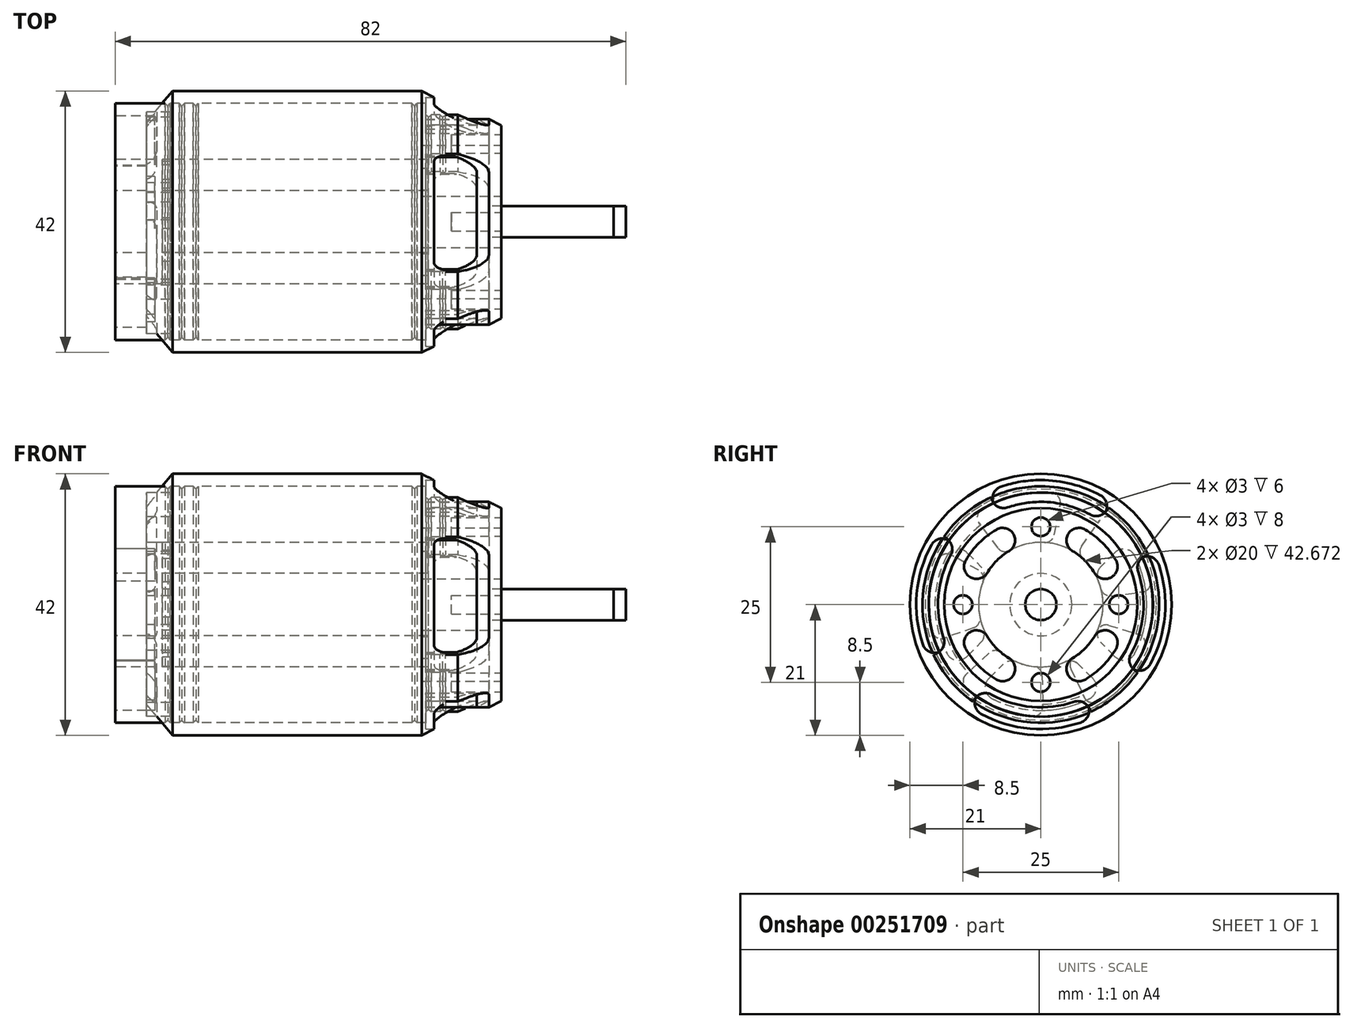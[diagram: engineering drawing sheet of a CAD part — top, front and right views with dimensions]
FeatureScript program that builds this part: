
annotation { "Feature Type Name" : "Feature", "Feature Type Description" : "" }
export const myFeature = defineFeature(function(context is Context, id is Id, definition is map)
    precondition{}
    {
        {
            var Q0;
            Q0=qCreatedBy(makeId("Top.planeOp"),FACE);
            var sketch = newSketch(context, id + "F0", { "sketchPlane" : qUnion([Q0])});
            skLineSegment(sketch, "E0", {"start": v(0, 0) * mm, "end": v(82, 0) * mm});
            skLineSegment(sketch, "E1", {"start": v(82, 0) * mm, "end": v(82, 2.5) * mm});
            skLineSegment(sketch, "E2", {"start": v(82, 2.5) * mm, "end": v(62, 2.5) * mm});
            skLineSegment(sketch, "E3", {"start": v(62, 2.5) * mm, "end": v(62, 15.5) * mm});
            skLineSegment(sketch, "E4", {"start": v(62, 15.5) * mm, "end": v(55, 19) * mm});
            skLineSegment(sketch, "E5", {"start": v(55, 19) * mm, "end": v(0, 19) * mm});
            skLineSegment(sketch, "E6", {"start": v(0, 19) * mm, "end": v(0, 0) * mm});
            skLineSegment(sketch, "E7", {"start": v(53, 19) * mm, "end": v(52.58, 18.58) * mm});
            skLineSegment(sketch, "E8", {"start": v(52.58, 18.58) * mm, "end": v(52.15, 19) * mm});
            skLineSegment(sketch, "E9.1.0.0", {"start": v(50.74, 19) * mm, "end": v(50.32, 18.58) * mm});
            skLineSegment(sketch, "E9.1.0.1", {"start": v(50.32, 18.58) * mm, "end": v(49.9, 19) * mm});
            skLineSegment(sketch, "E9.2.0.0", {"start": v(48.48, 19) * mm, "end": v(48.05, 18.58) * mm});
            skLineSegment(sketch, "E9.2.0.1", {"start": v(48.05, 18.58) * mm, "end": v(47.63, 19) * mm});
            skLineSegment(sketch, "E9.direction1", {"start": v(52.58, 18.58) * mm, "end": v(50.32, 18.58) * mm, "construction": true});
            skLineSegment(sketch, "E10", {"start": v(6, 19) * mm, "end": v(6, 0) * mm, "construction": true});
            skLineSegment(sketch, "E11", {"start": v(30.5, 19) * mm, "end": v(30.5, 0) * mm, "construction": true});
            skLineSegment(sketch, "E12.MirrorCS", {"start": v(8, 19) * mm, "end": v(8.42, 18.58) * mm});
            skLineSegment(sketch, "E13.MirrorCS", {"start": v(8.42, 18.58) * mm, "end": v(8.85, 19) * mm});
            skLineSegment(sketch, "E14.MirrorCS", {"start": v(10.26, 19) * mm, "end": v(10.68, 18.58) * mm});
            skLineSegment(sketch, "E15.MirrorCS", {"start": v(10.68, 18.58) * mm, "end": v(11.1, 19) * mm});
            skLineSegment(sketch, "E16.MirrorCS", {"start": v(12.52, 19) * mm, "end": v(12.95, 18.58) * mm});
            skLineSegment(sketch, "E17.MirrorCS", {"start": v(12.95, 18.58) * mm, "end": v(13.37, 19) * mm});
            skSolve(sketch);
        }
        {
            var Q0;
            Q0=makeQuery(id+"F0.imprint","IMPRINT",FACE,{"disambiguationData":[TD([[makeQuery(id+"F0.imprint","IMPRINT",EDGE,{"derivedFrom":sQuery(id+"F0.wireOp",EDGE,"E0")}),1.0]])]});
            var Q1;
            Q1=sQuery(id+"F0.wireOp",EDGE,"E0");
            revolve(context, id + "F1", {"entities" : qUnion([Q0]), "axis" : qUnion([Q1]), "revolveType" : RevolveType.FULL});
        }
        {
            var Q0;
            Q0=makeQuery(id+"F1.opRevolve","SWEPT_FACE",FACE,{"disambiguationData":[OSD([sQuery(id+"F0.wireOp",EDGE,"E3")])]});
            var sketch = newSketch(context, id + "F2", { "sketchPlane" : qUnion([Q0])});
            skCircle(sketch, "E18", {"center": v(0, 0) * mm, "radius": 12.5 * mm, "construction": true});
            skCircle(sketch, "E19", {"center": v(0, 12.5) * mm, "radius": 1.5 * mm});
            skCircle(sketch, "E20.1.0", {"center": v(-12.5, 0) * mm, "radius": 1.5 * mm});
            skCircle(sketch, "E20.2.0", {"center": v(0, -12.5) * mm, "radius": 1.5 * mm});
            skCircle(sketch, "E20.3.0", {"center": v(12.5, 0) * mm, "radius": 1.5 * mm});
            skCircle(sketch, "E21", {"center": v(0, 0) * mm, "radius": 14 * mm});
            skCircle(sketch, "E22", {"center": v(0, 0) * mm, "radius": 10 * mm});
            skLineSegment(sketch, "E23", {"start": v(-9.33, 3.6) * mm, "end": v(-13.06, 5.04) * mm});
            skLineSegment(sketch, "E24", {"start": v(-3.6, 9.33) * mm, "end": v(-5.04, 13.06) * mm});
            skLineSegment(sketch, "E25.1.0", {"start": v(-3.6, -9.33) * mm, "end": v(-5.04, -13.06) * mm});
            skLineSegment(sketch, "E25.1.1", {"start": v(-9.33, -3.6) * mm, "end": v(-13.06, -5.04) * mm});
            skLineSegment(sketch, "E25.2.0", {"start": v(9.33, -3.6) * mm, "end": v(13.06, -5.04) * mm});
            skLineSegment(sketch, "E25.2.1", {"start": v(3.6, -9.33) * mm, "end": v(5.04, -13.06) * mm});
            skLineSegment(sketch, "E25.3.0", {"start": v(3.6, 9.33) * mm, "end": v(5.04, 13.06) * mm});
            skLineSegment(sketch, "E25.3.1", {"start": v(9.33, 3.6) * mm, "end": v(13.06, 5.04) * mm});
            skSolve(sketch);
        }
        {
            var Q0;
            Q0=makeQuery(id+"F2.imprint","IMPRINT",FACE,{"disambiguationData":[TD([[makeQuery(id+"F2.imprint","IMPRINT",EDGE,{"derivedFrom":sQuery(id+"F2.wireOp",EDGE,"E20.1.0")}),1.0]])]});
            var Q1;
            Q1=makeQuery(id+"F2.imprint","IMPRINT",FACE,{"disambiguationData":[TD([[makeQuery(id+"F2.imprint","IMPRINT",EDGE,{"derivedFrom":sQuery(id+"F2.wireOp",EDGE,"E19")}),1.0]])]});
            var Q2;
            Q2=makeQuery(id+"F2.imprint","IMPRINT",FACE,{"disambiguationData":[TD([[makeQuery(id+"F2.imprint","IMPRINT",EDGE,{"derivedFrom":sQuery(id+"F2.wireOp",EDGE,"E20.3.0")}),1.0]])]});
            var Q3;
            Q3=makeQuery(id+"F2.imprint","IMPRINT",FACE,{"disambiguationData":[TD([[makeQuery(id+"F2.imprint","IMPRINT",EDGE,{"derivedFrom":sQuery(id+"F2.wireOp",EDGE,"E20.2.0")}),1.0]])]});
            extrude(context, id + "F3", {"entities" : qUnion([Q0, Q1, Q2, Q3]), "operationType" : NewBodyOperationType.REMOVE, "oppositeDirection" : true, "depth" : 6 * mm});
        }
        {
            var Q0;
            {var subQ0=sQuery(id+"F2.wireOp",EDGE,"E23");Q0=makeQuery(id+"F2.imprint","IMPRINT",FACE,{"disambiguationData":[TD([[makeQuery(id+"F2.imprint","IMPRINT",EDGE,{"derivedFrom":subQ0}),-1.0]])]});}
            var Q1;
            {var subQ0=sQuery(id+"F2.wireOp",EDGE,"E25.3.0");Q1=makeQuery(id+"F2.imprint","IMPRINT",FACE,{"disambiguationData":[TD([[makeQuery(id+"F2.imprint","IMPRINT",EDGE,{"derivedFrom":subQ0}),-1.0]])]});}
            var Q2;
            {var subQ0=sQuery(id+"F2.wireOp",EDGE,"E25.2.0");Q2=makeQuery(id+"F2.imprint","IMPRINT",FACE,{"disambiguationData":[TD([[makeQuery(id+"F2.imprint","IMPRINT",EDGE,{"derivedFrom":subQ0}),-1.0]])]});}
            var Q3;
            {var subQ0=sQuery(id+"F2.wireOp",EDGE,"E25.1.0");Q3=makeQuery(id+"F2.imprint","IMPRINT",FACE,{"disambiguationData":[TD([[makeQuery(id+"F2.imprint","IMPRINT",EDGE,{"derivedFrom":subQ0}),-1.0]])]});}
            extrude(context, id + "F4", {"entities" : qUnion([Q0, Q1, Q2, Q3]), "operationType" : NewBodyOperationType.REMOVE, "oppositeDirection" : true, "depth" : 12.7 * mm});
        }
        {
            var Q0;
            Q0=makeQuery(id+"F4.boolean.opBoolean","COPY",EDGE,{"derivedFrom":makeQuery(id+"F4.opExtrude","SWEPT_EDGE",EDGE,{"disambiguationData":[OSD([sQuery(id+"F2.wireOp",EDGE,"E21"),sQuery(id+"F2.wireOp",EDGE,"E23")])]})});
            var Q1;
            Q1=makeQuery(id+"F4.boolean.opBoolean","COPY",EDGE,{"derivedFrom":makeQuery(id+"F4.opExtrude","SWEPT_EDGE",EDGE,{"disambiguationData":[OSD([sQuery(id+"F2.wireOp",EDGE,"E22"),sQuery(id+"F2.wireOp",EDGE,"E23")])]})});
            var Q2;
            Q2=makeQuery(id+"F4.boolean.opBoolean","COPY",EDGE,{"derivedFrom":makeQuery(id+"F4.opExtrude","SWEPT_EDGE",EDGE,{"disambiguationData":[OSD([sQuery(id+"F2.wireOp",EDGE,"E21"),sQuery(id+"F2.wireOp",EDGE,"E24")])]})});
            var Q3;
            Q3=makeQuery(id+"F4.boolean.opBoolean","COPY",EDGE,{"derivedFrom":makeQuery(id+"F4.opExtrude","SWEPT_EDGE",EDGE,{"disambiguationData":[OSD([sQuery(id+"F2.wireOp",EDGE,"E22"),sQuery(id+"F2.wireOp",EDGE,"E24")])]})});
            var Q4;
            Q4=makeQuery(id+"F4.boolean.opBoolean","COPY",EDGE,{"derivedFrom":makeQuery(id+"F4.opExtrude","SWEPT_EDGE",EDGE,{"disambiguationData":[OSD([sQuery(id+"F2.wireOp",EDGE,"E21"),sQuery(id+"F2.wireOp",EDGE,"E25.3.0")])]})});
            var Q5;
            Q5=makeQuery(id+"F4.boolean.opBoolean","COPY",EDGE,{"derivedFrom":makeQuery(id+"F4.opExtrude","SWEPT_EDGE",EDGE,{"disambiguationData":[OSD([sQuery(id+"F2.wireOp",EDGE,"E22"),sQuery(id+"F2.wireOp",EDGE,"E25.2.0")])]})});
            var Q6;
            Q6=makeQuery(id+"F4.boolean.opBoolean","COPY",EDGE,{"derivedFrom":makeQuery(id+"F4.opExtrude","SWEPT_EDGE",EDGE,{"disambiguationData":[OSD([sQuery(id+"F2.wireOp",EDGE,"E22"),sQuery(id+"F2.wireOp",EDGE,"E25.1.1")])]})});
            var Q7;
            Q7=makeQuery(id+"F4.boolean.opBoolean","COPY",EDGE,{"derivedFrom":makeQuery(id+"F4.opExtrude","SWEPT_EDGE",EDGE,{"disambiguationData":[OSD([sQuery(id+"F2.wireOp",EDGE,"E22"),sQuery(id+"F2.wireOp",EDGE,"E25.2.1")])]})});
            var Q8;
            Q8=makeQuery(id+"F4.boolean.opBoolean","COPY",EDGE,{"derivedFrom":makeQuery(id+"F4.opExtrude","SWEPT_EDGE",EDGE,{"disambiguationData":[OSD([sQuery(id+"F2.wireOp",EDGE,"E22"),sQuery(id+"F2.wireOp",EDGE,"E25.1.0")])]})});
            var Q9;
            Q9=makeQuery(id+"F4.boolean.opBoolean","COPY",EDGE,{"derivedFrom":makeQuery(id+"F4.opExtrude","SWEPT_EDGE",EDGE,{"disambiguationData":[OSD([sQuery(id+"F2.wireOp",EDGE,"E21"),sQuery(id+"F2.wireOp",EDGE,"E25.2.0")])]})});
            var Q10;
            Q10=makeQuery(id+"F4.boolean.opBoolean","COPY",EDGE,{"derivedFrom":makeQuery(id+"F4.opExtrude","SWEPT_EDGE",EDGE,{"disambiguationData":[OSD([sQuery(id+"F2.wireOp",EDGE,"E21"),sQuery(id+"F2.wireOp",EDGE,"E25.2.1")])]})});
            var Q11;
            Q11=makeQuery(id+"F4.boolean.opBoolean","COPY",EDGE,{"derivedFrom":makeQuery(id+"F4.opExtrude","SWEPT_EDGE",EDGE,{"disambiguationData":[OSD([sQuery(id+"F2.wireOp",EDGE,"E21"),sQuery(id+"F2.wireOp",EDGE,"E25.1.0")])]})});
            var Q12;
            Q12=makeQuery(id+"F4.boolean.opBoolean","COPY",EDGE,{"derivedFrom":makeQuery(id+"F4.opExtrude","SWEPT_EDGE",EDGE,{"disambiguationData":[OSD([sQuery(id+"F2.wireOp",EDGE,"E22"),sQuery(id+"F2.wireOp",EDGE,"E25.3.1")])]})});
            var Q13;
            Q13=makeQuery(id+"F4.boolean.opBoolean","COPY",EDGE,{"derivedFrom":makeQuery(id+"F4.opExtrude","SWEPT_EDGE",EDGE,{"disambiguationData":[OSD([sQuery(id+"F2.wireOp",EDGE,"E22"),sQuery(id+"F2.wireOp",EDGE,"E25.3.0")])]})});
            var Q14;
            Q14=makeQuery(id+"F4.boolean.opBoolean","COPY",EDGE,{"derivedFrom":makeQuery(id+"F4.opExtrude","SWEPT_EDGE",EDGE,{"disambiguationData":[OSD([sQuery(id+"F2.wireOp",EDGE,"E21"),sQuery(id+"F2.wireOp",EDGE,"E25.1.1")])]})});
            var Q15;
            Q15=makeQuery(id+"F4.boolean.opBoolean","COPY",EDGE,{"derivedFrom":makeQuery(id+"F4.opExtrude","SWEPT_EDGE",EDGE,{"disambiguationData":[OSD([sQuery(id+"F2.wireOp",EDGE,"E21"),sQuery(id+"F2.wireOp",EDGE,"E25.3.1")])]})});
            fillet(context, id + "F5", {"entities" : qUnion([Q0, Q1, Q2, Q3, Q4, Q5, Q6, Q7, Q8, Q9, Q10, Q11, Q12, Q13, Q14, Q15]), "radius" : 2 * mm, "tangentPropagation" : true, "allowEdgeOverflow" : false});
        }
        {
            var Q0;
            Q0=makeQuery(id+"F1.opRevolve","SWEPT_FACE",FACE,{"disambiguationData":[OSD([sQuery(id+"F0.wireOp",EDGE,"E6")])]});
            var sketch = newSketch(context, id + "F6", { "sketchPlane" : qUnion([Q0])});
            skCircle(sketch, "E26", {"center": v(0, 0) * mm, "radius": 5 * mm});
            skCircle(sketch, "E27", {"center": v(0, 0) * mm, "radius": 17 * mm});
            skCircle(sketch, "E28", {"center": v(0, 0) * mm, "radius": 10 * mm});
            skLineSegment(sketch, "E29", {"start": v(-7.07, 7.07) * mm, "end": v(-12.02, 12.02) * mm, "construction": true});
            skLineSegment(sketch, "E30", {"start": v(0, 0) * mm, "end": v(-19, 0) * mm, "construction": true});
            skLineSegment(sketch, "E31", {"start": v(-10.12, 13.66) * mm, "end": v(-5.08, 8.61) * mm});
            skLineSegment(sketch, "E32.MirrorCS", {"start": v(-13.66, 10.12) * mm, "end": v(-8.61, 5.08) * mm});
            skLineSegment(sketch, "E33.1.0", {"start": v(-13.66, -10.12) * mm, "end": v(-8.61, -5.08) * mm});
            skLineSegment(sketch, "E33.1.1", {"start": v(-10.12, -13.66) * mm, "end": v(-5.08, -8.61) * mm});
            skLineSegment(sketch, "E33.2.0", {"start": v(10.12, -13.66) * mm, "end": v(5.08, -8.61) * mm});
            skLineSegment(sketch, "E33.2.1", {"start": v(13.66, -10.12) * mm, "end": v(8.61, -5.08) * mm});
            skLineSegment(sketch, "E33.3.0", {"start": v(13.66, 10.12) * mm, "end": v(8.61, 5.08) * mm});
            skLineSegment(sketch, "E33.3.1", {"start": v(10.12, 13.66) * mm, "end": v(5.08, 8.61) * mm});
            skSolve(sketch);
        }
        {
            var Q0;
            {var subQ0=sQuery(id+"F6.wireOp",EDGE,"E32.MirrorCS");Q0=makeQuery(id+"F6.imprint","IMPRINT",FACE,{"disambiguationData":[TD([[makeQuery(id+"F6.imprint","IMPRINT",EDGE,{"derivedFrom":subQ0}),-1.0]])]});}
            var Q1;
            {var subQ0=sQuery(id+"F6.wireOp",EDGE,"E33.2.1");Q1=makeQuery(id+"F6.imprint","IMPRINT",FACE,{"disambiguationData":[TD([[makeQuery(id+"F6.imprint","IMPRINT",EDGE,{"derivedFrom":subQ0}),-1.0]])]});}
            var Q2;
            {var subQ0=sQuery(id+"F6.wireOp",EDGE,"E33.1.1");Q2=makeQuery(id+"F6.imprint","IMPRINT",FACE,{"disambiguationData":[TD([[makeQuery(id+"F6.imprint","IMPRINT",EDGE,{"derivedFrom":subQ0}),-1.0]])]});}
            extrude(context, id + "F7", {"entities" : qUnion([Q0, Q1, Q2]), "operationType" : NewBodyOperationType.REMOVE, "oppositeDirection" : true, "depth" : 6.35 * mm});
        }
        {
            var Q0;
            Q0=makeQuery(id+"F7.boolean.opBoolean","COPY",EDGE,{"derivedFrom":makeQuery(id+"F7.opExtrude","SWEPT_EDGE",EDGE,{"disambiguationData":[OSD([sQuery(id+"F6.wireOp",EDGE,"E27"),sQuery(id+"F6.wireOp",EDGE,"E32.MirrorCS")])]})});
            var Q1;
            Q1=makeQuery(id+"F7.boolean.opBoolean","COPY",EDGE,{"derivedFrom":makeQuery(id+"F7.opExtrude","SWEPT_EDGE",EDGE,{"disambiguationData":[OSD([sQuery(id+"F6.wireOp",EDGE,"E27"),sQuery(id+"F6.wireOp",EDGE,"E33.3.0")])]})});
            var Q2;
            Q2=makeQuery(id+"F7.boolean.opBoolean","COPY",EDGE,{"derivedFrom":makeQuery(id+"F7.opExtrude","SWEPT_EDGE",EDGE,{"disambiguationData":[OSD([sQuery(id+"F6.wireOp",EDGE,"E28"),sQuery(id+"F6.wireOp",EDGE,"E33.1.1")])]})});
            var Q3;
            Q3=makeQuery(id+"F7.boolean.opBoolean","COPY",EDGE,{"derivedFrom":makeQuery(id+"F7.opExtrude","SWEPT_EDGE",EDGE,{"disambiguationData":[OSD([sQuery(id+"F6.wireOp",EDGE,"E28"),sQuery(id+"F6.wireOp",EDGE,"E33.2.0")])]})});
            var Q4;
            Q4=makeQuery(id+"F7.boolean.opBoolean","COPY",EDGE,{"derivedFrom":makeQuery(id+"F7.opExtrude","SWEPT_EDGE",EDGE,{"disambiguationData":[OSD([sQuery(id+"F6.wireOp",EDGE,"E28"),sQuery(id+"F6.wireOp",EDGE,"E33.2.1")])]})});
            var Q5;
            Q5=makeQuery(id+"F7.boolean.opBoolean","COPY",EDGE,{"derivedFrom":makeQuery(id+"F7.opExtrude","SWEPT_EDGE",EDGE,{"disambiguationData":[OSD([sQuery(id+"F6.wireOp",EDGE,"E27"),sQuery(id+"F6.wireOp",EDGE,"E33.1.1")])]})});
            var Q6;
            Q6=makeQuery(id+"F7.boolean.opBoolean","COPY",EDGE,{"derivedFrom":makeQuery(id+"F7.opExtrude","SWEPT_EDGE",EDGE,{"disambiguationData":[OSD([sQuery(id+"F6.wireOp",EDGE,"E27"),sQuery(id+"F6.wireOp",EDGE,"E33.2.1")])]})});
            var Q7;
            Q7=makeQuery(id+"F7.boolean.opBoolean","COPY",EDGE,{"derivedFrom":makeQuery(id+"F7.opExtrude","SWEPT_EDGE",EDGE,{"disambiguationData":[OSD([sQuery(id+"F6.wireOp",EDGE,"E28"),sQuery(id+"F6.wireOp",EDGE,"E33.3.0")])]})});
            var Q8;
            Q8=makeQuery(id+"F7.boolean.opBoolean","COPY",EDGE,{"derivedFrom":makeQuery(id+"F7.opExtrude","SWEPT_EDGE",EDGE,{"disambiguationData":[OSD([sQuery(id+"F6.wireOp",EDGE,"E27"),sQuery(id+"F6.wireOp",EDGE,"E33.2.0")])]})});
            var Q9;
            Q9=makeQuery(id+"F7.boolean.opBoolean","COPY",EDGE,{"derivedFrom":makeQuery(id+"F7.opExtrude","SWEPT_EDGE",EDGE,{"disambiguationData":[OSD([sQuery(id+"F6.wireOp",EDGE,"E28"),sQuery(id+"F6.wireOp",EDGE,"E32.MirrorCS")])]})});
            var Q10;
            Q10=makeQuery(id+"F7.boolean.opBoolean","COPY",EDGE,{"derivedFrom":makeQuery(id+"F7.opExtrude","SWEPT_EDGE",EDGE,{"disambiguationData":[OSD([sQuery(id+"F6.wireOp",EDGE,"E28"),sQuery(id+"F6.wireOp",EDGE,"E33.1.0")])]})});
            var Q11;
            Q11=makeQuery(id+"F7.boolean.opBoolean","COPY",EDGE,{"derivedFrom":makeQuery(id+"F7.opExtrude","SWEPT_EDGE",EDGE,{"disambiguationData":[OSD([sQuery(id+"F6.wireOp",EDGE,"E27"),sQuery(id+"F6.wireOp",EDGE,"E33.1.0")])]})});
            fillet(context, id + "F8", {"entities" : qUnion([Q0, Q1, Q2, Q3, Q4, Q5, Q6, Q7, Q8, Q9, Q10, Q11]), "radius" : 2 * mm, "tangentPropagation" : true, "allowEdgeOverflow" : false});
        }
        {
            var Q0;
            Q0=qCreatedBy(makeId("Top.planeOp"),FACE);
            var sketch = newSketch(context, id + "F9", { "sketchPlane" : qUnion([Q0])});
            skLineSegment(sketch, "E34", {"start": v(0, 0) * mm, "end": v(80, 0) * mm});
            skLineSegment(sketch, "E35", {"start": v(80, 0) * mm, "end": v(80, 2.5) * mm});
            skLineSegment(sketch, "E36", {"start": v(80, 2.5) * mm, "end": v(60, 2.5) * mm});
            skLineSegment(sketch, "E37", {"start": v(60, 2.5) * mm, "end": v(60, 15.5) * mm});
            skLineSegment(sketch, "E38", {"start": v(60, 15.5) * mm, "end": v(49.2, 21) * mm});
            skLineSegment(sketch, "E39", {"start": v(49.2, 21) * mm, "end": v(9.2, 21) * mm});
            skLineSegment(sketch, "E40", {"start": v(9.2, 21) * mm, "end": v(5, 16) * mm});
            skLineSegment(sketch, "E41", {"start": v(5, 16) * mm, "end": v(5, 5) * mm});
            skLineSegment(sketch, "E42", {"start": v(5, 5) * mm, "end": v(0, 5) * mm});
            skLineSegment(sketch, "E43", {"start": v(0, 5) * mm, "end": v(0, 0) * mm});
            skSolve(sketch);
        }
        {
            var Q0;
            Q0=makeQuery(id+"F9.imprint","IMPRINT",FACE,{"disambiguationData":[TD([[makeQuery(id+"F9.imprint","IMPRINT",EDGE,{"derivedFrom":sQuery(id+"F9.wireOp",EDGE,"E34")}),1.0]])]});
            var Q1;
            Q1=sQuery(id+"F9.wireOp",EDGE,"E34");
            revolve(context, id + "F10", {"entities" : qUnion([Q0]), "axis" : qUnion([Q1]), "revolveType" : RevolveType.FULL});
        }
        {
            var Q0;
            Q0=makeQuery(id+"F10.opRevolve","SWEPT_FACE",FACE,{"disambiguationData":[OSD([sQuery(id+"F9.wireOp",EDGE,"E37")])]});
            var sketch = newSketch(context, id + "F11", { "sketchPlane" : qUnion([Q0])});
            skCircle(sketch, "E44", {"center": v(0, 0) * mm, "radius": 12.5 * mm, "construction": true});
            skCircle(sketch, "E45", {"center": v(0, 12.5) * mm, "radius": 1.5 * mm});
            skCircle(sketch, "E46.1.0", {"center": v(-12.5, 0) * mm, "radius": 1.5 * mm});
            skCircle(sketch, "E46.2.0", {"center": v(0, -12.5) * mm, "radius": 1.5 * mm});
            skCircle(sketch, "E46.3.0", {"center": v(12.5, 0) * mm, "radius": 1.5 * mm});
            skCircle(sketch, "E47", {"center": v(0, 0) * mm, "radius": 20 * mm});
            skCircle(sketch, "E48", {"center": v(0, 0) * mm, "radius": 16.5 * mm});
            skLineSegment(sketch, "E49", {"start": v(9.46, 13.52) * mm, "end": v(11.47, 16.39) * mm});
            skLineSegment(sketch, "E50", {"start": v(14.95, 6.98) * mm, "end": v(18.12, 8.46) * mm});
            skCircle(sketch, "E51.0", {"center": v(0, 0) * mm, "radius": 15.5 * mm, "construction": true});
            skLineSegment(sketch, "E52.1.0", {"start": v(-13.52, 9.46) * mm, "end": v(-16.39, 11.47) * mm});
            skLineSegment(sketch, "E52.1.1", {"start": v(-6.98, 14.95) * mm, "end": v(-8.46, 18.12) * mm});
            skLineSegment(sketch, "E52.2.0", {"start": v(-9.46, -13.52) * mm, "end": v(-11.47, -16.39) * mm});
            skLineSegment(sketch, "E52.2.1", {"start": v(-14.95, -6.98) * mm, "end": v(-18.12, -8.46) * mm});
            skLineSegment(sketch, "E52.3.0", {"start": v(13.52, -9.46) * mm, "end": v(16.39, -11.47) * mm});
            skLineSegment(sketch, "E52.3.1", {"start": v(6.98, -14.95) * mm, "end": v(8.46, -18.12) * mm});
            skSolve(sketch);
        }
        {
            var Q0;
            Q0=makeQuery(id+"F10.opRevolve","SWEPT_FACE",FACE,{"disambiguationData":[OSD([sQuery(id+"F9.wireOp",EDGE,"E41")])]});
            var sketch = newSketch(context, id + "F12", { "sketchPlane" : qUnion([Q0])});
            skCircle(sketch, "E53.0", {"center": v(0, 0) * mm, "radius": 21 * mm});
            skCircle(sketch, "E54", {"center": v(0, 0) * mm, "radius": 18 * mm});
            skCircle(sketch, "E55", {"center": v(0, 0) * mm, "radius": 10 * mm});
            skLineSegment(sketch, "E56", {"start": v(-1.9, 9.82) * mm, "end": v(-3.41, 17.67) * mm});
            skLineSegment(sketch, "E57", {"start": v(6.03, 7.98) * mm, "end": v(10.85, 14.36) * mm});
            skLineSegment(sketch, "E58.1.0", {"start": v(-9.92, 1.23) * mm, "end": v(-17.86, 2.21) * mm});
            skLineSegment(sketch, "E58.1.1", {"start": v(-5.73, 8.2) * mm, "end": v(-10.3, 14.76) * mm});
            skLineSegment(sketch, "E58.2.0", {"start": v(-4.24, -9.06) * mm, "end": v(-7.63, -16.3) * mm});
            skLineSegment(sketch, "E58.2.1", {"start": v(-9.57, -2.91) * mm, "end": v(-17.22, -5.24) * mm});
            skLineSegment(sketch, "E58.3.0", {"start": v(7.3, -6.83) * mm, "end": v(13.15, -12.3) * mm});
            skLineSegment(sketch, "E58.3.1", {"start": v(-0.19, -10) * mm, "end": v(-0.33, -18) * mm});
            skLineSegment(sketch, "E58.4.0", {"start": v(8.75, 4.84) * mm, "end": v(15.75, 8.7) * mm});
            skLineSegment(sketch, "E58.4.1", {"start": v(9.45, -3.27) * mm, "end": v(17.01, -5.88) * mm});
            skSolve(sketch);
        }
        {
            var Q0;
            {var subQ0=sQuery(id+"F12.wireOp",EDGE,"E56");var subQ1=sQuery(id+"F12.wireOp",EDGE,"E55");var subQ2=makeQuery(id+"F12.imprint","INTERSECT",VERTEX,{"derivedFrom":[subQ1,subQ0]});Q0=makeQuery(id+"F12.imprint","IMPRINT",FACE,{"disambiguationData":[TD([[makeQuery(id+"F12.imprint","IMPRINT",EDGE,{"disambiguationData":[TD([[subQ2,1.0]])],"derivedFrom":subQ1}),-1.0]])]});}
            var Q1;
            {var subQ0=sQuery(id+"F12.wireOp",EDGE,"E56");var subQ1=sQuery(id+"F12.wireOp",EDGE,"E54");var subQ2=makeQuery(id+"F12.imprint","INTERSECT",VERTEX,{"derivedFrom":[subQ1,subQ0]});Q1=makeQuery(id+"F12.imprint","IMPRINT",FACE,{"disambiguationData":[TD([[makeQuery(id+"F12.imprint","IMPRINT",EDGE,{"disambiguationData":[TD([[subQ2,1.0]])],"derivedFrom":subQ1}),1.0]])]});}
            var Q2;
            {var subQ0=sQuery(id+"F12.wireOp",EDGE,"E58.1.0");var subQ1=sQuery(id+"F12.wireOp",EDGE,"E55");var subQ2=makeQuery(id+"F12.imprint","INTERSECT",VERTEX,{"derivedFrom":[subQ1,subQ0]});Q2=makeQuery(id+"F12.imprint","IMPRINT",FACE,{"disambiguationData":[TD([[makeQuery(id+"F12.imprint","IMPRINT",EDGE,{"disambiguationData":[TD([[subQ2,1.0]])],"derivedFrom":subQ1}),-1.0]])]});}
            var Q3;
            {var subQ0=sQuery(id+"F12.wireOp",EDGE,"E58.1.0");var subQ1=sQuery(id+"F12.wireOp",EDGE,"E54");var subQ2=makeQuery(id+"F12.imprint","INTERSECT",VERTEX,{"derivedFrom":[subQ1,subQ0]});Q3=makeQuery(id+"F12.imprint","IMPRINT",FACE,{"disambiguationData":[TD([[makeQuery(id+"F12.imprint","IMPRINT",EDGE,{"disambiguationData":[TD([[subQ2,1.0]])],"derivedFrom":subQ1}),1.0]])]});}
            var Q4;
            {var subQ0=sQuery(id+"F12.wireOp",EDGE,"E58.2.0");var subQ1=sQuery(id+"F12.wireOp",EDGE,"E55");var subQ2=makeQuery(id+"F12.imprint","INTERSECT",VERTEX,{"derivedFrom":[subQ1,subQ0]});Q4=makeQuery(id+"F12.imprint","IMPRINT",FACE,{"disambiguationData":[TD([[makeQuery(id+"F12.imprint","IMPRINT",EDGE,{"disambiguationData":[TD([[subQ2,1.0]])],"derivedFrom":subQ1}),-1.0]])]});}
            var Q5;
            {var subQ0=sQuery(id+"F12.wireOp",EDGE,"E58.3.0");var subQ1=sQuery(id+"F12.wireOp",EDGE,"E55");var subQ2=makeQuery(id+"F12.imprint","INTERSECT",VERTEX,{"derivedFrom":[subQ1,subQ0]});Q5=makeQuery(id+"F12.imprint","IMPRINT",FACE,{"disambiguationData":[TD([[makeQuery(id+"F12.imprint","IMPRINT",EDGE,{"disambiguationData":[TD([[subQ2,1.0]])],"derivedFrom":subQ1}),-1.0]])]});}
            var Q6;
            {var subQ0=sQuery(id+"F12.wireOp",EDGE,"E58.4.0");var subQ1=sQuery(id+"F12.wireOp",EDGE,"E55");var subQ2=makeQuery(id+"F12.imprint","INTERSECT",VERTEX,{"derivedFrom":[subQ1,subQ0]});Q6=makeQuery(id+"F12.imprint","IMPRINT",FACE,{"disambiguationData":[TD([[makeQuery(id+"F12.imprint","IMPRINT",EDGE,{"disambiguationData":[TD([[subQ2,1.0]])],"derivedFrom":subQ1}),-1.0]])]});}
            var Q7;
            {var subQ0=sQuery(id+"F12.wireOp",EDGE,"E58.4.0");var subQ1=sQuery(id+"F12.wireOp",EDGE,"E54");var subQ2=makeQuery(id+"F12.imprint","INTERSECT",VERTEX,{"derivedFrom":[subQ1,subQ0]});Q7=makeQuery(id+"F12.imprint","IMPRINT",FACE,{"disambiguationData":[TD([[makeQuery(id+"F12.imprint","IMPRINT",EDGE,{"disambiguationData":[TD([[subQ2,1.0]])],"derivedFrom":subQ1}),1.0]])]});}
            var Q8;
            {var subQ0=sQuery(id+"F12.wireOp",EDGE,"E58.3.0");var subQ1=sQuery(id+"F12.wireOp",EDGE,"E54");var subQ2=makeQuery(id+"F12.imprint","INTERSECT",VERTEX,{"derivedFrom":[subQ1,subQ0]});Q8=makeQuery(id+"F12.imprint","IMPRINT",FACE,{"disambiguationData":[TD([[makeQuery(id+"F12.imprint","IMPRINT",EDGE,{"disambiguationData":[TD([[subQ2,1.0]])],"derivedFrom":subQ1}),1.0]])]});}
            var Q9;
            {var subQ0=sQuery(id+"F12.wireOp",EDGE,"E58.2.0");var subQ1=sQuery(id+"F12.wireOp",EDGE,"E54");var subQ2=makeQuery(id+"F12.imprint","INTERSECT",VERTEX,{"derivedFrom":[subQ1,subQ0]});Q9=makeQuery(id+"F12.imprint","IMPRINT",FACE,{"disambiguationData":[TD([[makeQuery(id+"F12.imprint","IMPRINT",EDGE,{"disambiguationData":[TD([[subQ2,1.0]])],"derivedFrom":subQ1}),1.0]])]});}
            extrude(context, id + "F13", {"entities" : qUnion([Q0, Q1, Q2, Q3, Q4, Q5, Q6, Q7, Q8, Q9]), "operationType" : NewBodyOperationType.REMOVE, "oppositeDirection" : true, "depth" : 3.8 * mm});
        }
        {
            var Q0;
            Q0=makeQuery(id+"F13.boolean.opBoolean","COPY",EDGE,{"derivedFrom":makeQuery(id+"F13.opExtrude","SWEPT_EDGE",EDGE,{"disambiguationData":[OSD([sQuery(id+"F12.wireOp",EDGE,"E54"),sQuery(id+"F12.wireOp",EDGE,"E56")])]})});
            var Q1;
            Q1=makeQuery(id+"F13.boolean.opBoolean","COPY",EDGE,{"derivedFrom":makeQuery(id+"F13.opExtrude","SWEPT_EDGE",EDGE,{"disambiguationData":[OSD([sQuery(id+"F12.wireOp",EDGE,"E54"),sQuery(id+"F12.wireOp",EDGE,"E57")])]})});
            var Q2;
            Q2=makeQuery(id+"F13.boolean.opBoolean","COPY",EDGE,{"derivedFrom":makeQuery(id+"F13.opExtrude","SWEPT_EDGE",EDGE,{"disambiguationData":[OSD([sQuery(id+"F12.wireOp",EDGE,"E55"),sQuery(id+"F12.wireOp",EDGE,"E56")])]})});
            var Q3;
            Q3=makeQuery(id+"F13.boolean.opBoolean","COPY",EDGE,{"derivedFrom":makeQuery(id+"F13.opExtrude","SWEPT_EDGE",EDGE,{"disambiguationData":[OSD([sQuery(id+"F12.wireOp",EDGE,"E55"),sQuery(id+"F12.wireOp",EDGE,"E57")])]})});
            var Q4;
            Q4=makeQuery(id+"F13.boolean.opBoolean","COPY",EDGE,{"derivedFrom":makeQuery(id+"F13.opExtrude","SWEPT_EDGE",EDGE,{"disambiguationData":[OSD([sQuery(id+"F12.wireOp",EDGE,"E54"),sQuery(id+"F12.wireOp",EDGE,"E58.1.1")])]})});
            var Q5;
            Q5=makeQuery(id+"F13.boolean.opBoolean","COPY",EDGE,{"derivedFrom":makeQuery(id+"F13.opExtrude","SWEPT_EDGE",EDGE,{"disambiguationData":[OSD([sQuery(id+"F12.wireOp",EDGE,"E55"),sQuery(id+"F12.wireOp",EDGE,"E58.2.1")])]})});
            var Q6;
            Q6=makeQuery(id+"F13.boolean.opBoolean","COPY",EDGE,{"derivedFrom":makeQuery(id+"F13.opExtrude","SWEPT_EDGE",EDGE,{"disambiguationData":[OSD([sQuery(id+"F12.wireOp",EDGE,"E54"),sQuery(id+"F12.wireOp",EDGE,"E58.4.0")])]})});
            var Q7;
            Q7=makeQuery(id+"F13.boolean.opBoolean","COPY",EDGE,{"derivedFrom":makeQuery(id+"F13.opExtrude","SWEPT_EDGE",EDGE,{"disambiguationData":[OSD([sQuery(id+"F12.wireOp",EDGE,"E55"),sQuery(id+"F12.wireOp",EDGE,"E58.3.0")])]})});
            var Q8;
            Q8=makeQuery(id+"F13.boolean.opBoolean","COPY",EDGE,{"derivedFrom":makeQuery(id+"F13.opExtrude","SWEPT_EDGE",EDGE,{"disambiguationData":[OSD([sQuery(id+"F12.wireOp",EDGE,"E54"),sQuery(id+"F12.wireOp",EDGE,"E58.1.0")])]})});
            var Q9;
            Q9=makeQuery(id+"F13.boolean.opBoolean","COPY",EDGE,{"derivedFrom":makeQuery(id+"F13.opExtrude","SWEPT_EDGE",EDGE,{"disambiguationData":[OSD([sQuery(id+"F12.wireOp",EDGE,"E55"),sQuery(id+"F12.wireOp",EDGE,"E58.4.1")])]})});
            var Q10;
            Q10=makeQuery(id+"F13.boolean.opBoolean","COPY",EDGE,{"derivedFrom":makeQuery(id+"F13.opExtrude","SWEPT_EDGE",EDGE,{"disambiguationData":[OSD([sQuery(id+"F12.wireOp",EDGE,"E55"),sQuery(id+"F12.wireOp",EDGE,"E58.4.0")])]})});
            var Q11;
            Q11=makeQuery(id+"F13.boolean.opBoolean","COPY",EDGE,{"derivedFrom":makeQuery(id+"F13.opExtrude","SWEPT_EDGE",EDGE,{"disambiguationData":[OSD([sQuery(id+"F12.wireOp",EDGE,"E55"),sQuery(id+"F12.wireOp",EDGE,"E58.3.1")])]})});
            var Q12;
            Q12=makeQuery(id+"F13.boolean.opBoolean","COPY",EDGE,{"derivedFrom":makeQuery(id+"F13.opExtrude","SWEPT_EDGE",EDGE,{"disambiguationData":[OSD([sQuery(id+"F12.wireOp",EDGE,"E54"),sQuery(id+"F12.wireOp",EDGE,"E58.2.1")])]})});
            var Q13;
            Q13=makeQuery(id+"F13.boolean.opBoolean","COPY",EDGE,{"derivedFrom":makeQuery(id+"F13.opExtrude","SWEPT_EDGE",EDGE,{"disambiguationData":[OSD([sQuery(id+"F12.wireOp",EDGE,"E54"),sQuery(id+"F12.wireOp",EDGE,"E58.2.0")])]})});
            var Q14;
            Q14=makeQuery(id+"F13.boolean.opBoolean","COPY",EDGE,{"derivedFrom":makeQuery(id+"F13.opExtrude","SWEPT_EDGE",EDGE,{"disambiguationData":[OSD([sQuery(id+"F12.wireOp",EDGE,"E54"),sQuery(id+"F12.wireOp",EDGE,"E58.4.1")])]})});
            var Q15;
            Q15=makeQuery(id+"F13.boolean.opBoolean","COPY",EDGE,{"derivedFrom":makeQuery(id+"F13.opExtrude","SWEPT_EDGE",EDGE,{"disambiguationData":[OSD([sQuery(id+"F12.wireOp",EDGE,"E54"),sQuery(id+"F12.wireOp",EDGE,"E58.3.0")])]})});
            var Q16;
            Q16=makeQuery(id+"F13.boolean.opBoolean","COPY",EDGE,{"derivedFrom":makeQuery(id+"F13.opExtrude","SWEPT_EDGE",EDGE,{"disambiguationData":[OSD([sQuery(id+"F12.wireOp",EDGE,"E54"),sQuery(id+"F12.wireOp",EDGE,"E58.3.1")])]})});
            var Q17;
            Q17=makeQuery(id+"F13.boolean.opBoolean","COPY",EDGE,{"derivedFrom":makeQuery(id+"F13.opExtrude","SWEPT_EDGE",EDGE,{"disambiguationData":[OSD([sQuery(id+"F12.wireOp",EDGE,"E55"),sQuery(id+"F12.wireOp",EDGE,"E58.1.0")])]})});
            var Q18;
            Q18=makeQuery(id+"F13.boolean.opBoolean","COPY",EDGE,{"derivedFrom":makeQuery(id+"F13.opExtrude","SWEPT_EDGE",EDGE,{"disambiguationData":[OSD([sQuery(id+"F12.wireOp",EDGE,"E55"),sQuery(id+"F12.wireOp",EDGE,"E58.1.1")])]})});
            var Q19;
            Q19=makeQuery(id+"F13.boolean.opBoolean","COPY",EDGE,{"derivedFrom":makeQuery(id+"F13.opExtrude","SWEPT_EDGE",EDGE,{"disambiguationData":[OSD([sQuery(id+"F12.wireOp",EDGE,"E55"),sQuery(id+"F12.wireOp",EDGE,"E58.2.0")])]})});
            fillet(context, id + "F14", {"entities" : qUnion([Q0, Q1, Q2, Q3, Q4, Q5, Q6, Q7, Q8, Q9, Q10, Q11, Q12, Q13, Q14, Q15, Q16, Q17, Q18, Q19]), "radius" : 1.5 * mm, "tangentPropagation" : true, "allowEdgeOverflow" : false});
        }
        {
            var Q0;
            Q0=makeQuery(id+"F11.imprint","IMPRINT",FACE,{"disambiguationData":[TD([[makeQuery(id+"F11.imprint","IMPRINT",EDGE,{"derivedFrom":sQuery(id+"F11.wireOp",EDGE,"E45")}),1.0]])]});
            var Q1;
            Q1=makeQuery(id+"F11.imprint","IMPRINT",FACE,{"disambiguationData":[TD([[makeQuery(id+"F11.imprint","IMPRINT",EDGE,{"derivedFrom":sQuery(id+"F11.wireOp",EDGE,"E46.1.0")}),1.0]])]});
            var Q2;
            Q2=makeQuery(id+"F11.imprint","IMPRINT",FACE,{"disambiguationData":[TD([[makeQuery(id+"F11.imprint","IMPRINT",EDGE,{"derivedFrom":sQuery(id+"F11.wireOp",EDGE,"E46.2.0")}),1.0]])]});
            var Q3;
            Q3=makeQuery(id+"F11.imprint","IMPRINT",FACE,{"disambiguationData":[TD([[makeQuery(id+"F11.imprint","IMPRINT",EDGE,{"derivedFrom":sQuery(id+"F11.wireOp",EDGE,"E46.3.0")}),1.0]])]});
            extrude(context, id + "F15", {"entities" : qUnion([Q0, Q1, Q2, Q3]), "operationType" : NewBodyOperationType.REMOVE, "oppositeDirection" : true, "depth" : 6 * mm});
        }
        {
            var Q0;
            {var subQ0=sQuery(id+"F11.wireOp",EDGE,"E49");Q0=makeQuery(id+"F11.imprint","IMPRINT",FACE,{"disambiguationData":[TD([[makeQuery(id+"F11.imprint","IMPRINT",EDGE,{"derivedFrom":subQ0}),1.0]])]});}
            var Q1;
            {var subQ0=sQuery(id+"F11.wireOp",EDGE,"E50");Q1=makeQuery(id+"F11.imprint","IMPRINT",FACE,{"disambiguationData":[TD([[makeQuery(id+"F11.imprint","IMPRINT",EDGE,{"derivedFrom":subQ0}),-1.0]])]});}
            var Q2;
            {var subQ0=sQuery(id+"F11.wireOp",EDGE,"E52.2.0");Q2=makeQuery(id+"F11.imprint","IMPRINT",FACE,{"disambiguationData":[TD([[makeQuery(id+"F11.imprint","IMPRINT",EDGE,{"derivedFrom":subQ0}),1.0]])]});}
            var Q3;
            {var subQ0=sQuery(id+"F11.wireOp",EDGE,"E52.1.0");Q3=makeQuery(id+"F11.imprint","IMPRINT",FACE,{"disambiguationData":[TD([[makeQuery(id+"F11.imprint","IMPRINT",EDGE,{"derivedFrom":subQ0}),1.0]])]});}
            extrude(context, id + "F16", {"entities" : qUnion([Q0, Q1, Q2, Q3]), "operationType" : NewBodyOperationType.REMOVE, "oppositeDirection" : true, "depth" : 10.16 * mm});
        }
        {
            var Q0;
            Q0=makeQuery(id+"F16.boolean.opBoolean","COPY",EDGE,{"derivedFrom":makeQuery(id+"F16.opExtrude","SWEPT_EDGE",EDGE,{"disambiguationData":[OSD([sQuery(id+"F11.wireOp",EDGE,"E48"),sQuery(id+"F11.wireOp",EDGE,"E52.2.1")])]})});
            var Q1;
            Q1=makeQuery(id+"F16.boolean.opBoolean","COPY",EDGE,{"derivedFrom":makeQuery(id+"F16.opExtrude","SWEPT_EDGE",EDGE,{"disambiguationData":[OSD([sQuery(id+"F11.wireOp",EDGE,"E47"),sQuery(id+"F11.wireOp",EDGE,"E52.2.1")])]})});
            var Q2;
            Q2=makeQuery(id+"F16.boolean.opBoolean","COPY",EDGE,{"derivedFrom":makeQuery(id+"F16.opExtrude","SWEPT_EDGE",EDGE,{"disambiguationData":[OSD([sQuery(id+"F11.wireOp",EDGE,"E47"),sQuery(id+"F11.wireOp",EDGE,"E52.1.0")])]})});
            var Q3;
            Q3=makeQuery(id+"F16.boolean.opBoolean","COPY",EDGE,{"derivedFrom":makeQuery(id+"F16.opExtrude","SWEPT_EDGE",EDGE,{"disambiguationData":[OSD([sQuery(id+"F11.wireOp",EDGE,"E48"),sQuery(id+"F11.wireOp",EDGE,"E52.1.0")])]})});
            var Q4;
            Q4=makeQuery(id+"F16.boolean.opBoolean","COPY",EDGE,{"derivedFrom":makeQuery(id+"F16.opExtrude","SWEPT_EDGE",EDGE,{"disambiguationData":[OSD([sQuery(id+"F11.wireOp",EDGE,"E47"),sQuery(id+"F11.wireOp",EDGE,"E52.1.1")])]})});
            var Q5;
            Q5=makeQuery(id+"F16.boolean.opBoolean","COPY",EDGE,{"derivedFrom":makeQuery(id+"F16.opExtrude","SWEPT_EDGE",EDGE,{"disambiguationData":[OSD([sQuery(id+"F11.wireOp",EDGE,"E48"),sQuery(id+"F11.wireOp",EDGE,"E52.1.1")])]})});
            var Q6;
            Q6=makeQuery(id+"F16.boolean.opBoolean","COPY",EDGE,{"derivedFrom":makeQuery(id+"F16.opExtrude","SWEPT_EDGE",EDGE,{"disambiguationData":[OSD([sQuery(id+"F11.wireOp",EDGE,"E48"),sQuery(id+"F11.wireOp",EDGE,"E49")])]})});
            var Q7;
            Q7=makeQuery(id+"F16.boolean.opBoolean","COPY",EDGE,{"derivedFrom":makeQuery(id+"F16.opExtrude","SWEPT_EDGE",EDGE,{"disambiguationData":[OSD([sQuery(id+"F11.wireOp",EDGE,"E48"),sQuery(id+"F11.wireOp",EDGE,"E50")])]})});
            var Q8;
            Q8=makeQuery(id+"F16.boolean.opBoolean","COPY",EDGE,{"derivedFrom":makeQuery(id+"F16.opExtrude","SWEPT_EDGE",EDGE,{"disambiguationData":[OSD([sQuery(id+"F11.wireOp",EDGE,"E48"),sQuery(id+"F11.wireOp",EDGE,"E52.3.0")])]})});
            var Q9;
            Q9=makeQuery(id+"F16.boolean.opBoolean","COPY",EDGE,{"derivedFrom":makeQuery(id+"F16.opExtrude","SWEPT_EDGE",EDGE,{"disambiguationData":[OSD([sQuery(id+"F11.wireOp",EDGE,"E48"),sQuery(id+"F11.wireOp",EDGE,"E52.2.0")])]})});
            var Q10;
            Q10=makeQuery(id+"F16.boolean.opBoolean","COPY",EDGE,{"derivedFrom":makeQuery(id+"F16.opExtrude","SWEPT_EDGE",EDGE,{"disambiguationData":[OSD([sQuery(id+"F11.wireOp",EDGE,"E48"),sQuery(id+"F11.wireOp",EDGE,"E52.3.1")])]})});
            var Q11;
            Q11=makeQuery(id+"F16.boolean.opBoolean","COPY",EDGE,{"derivedFrom":makeQuery(id+"F16.opExtrude","SWEPT_EDGE",EDGE,{"disambiguationData":[OSD([sQuery(id+"F11.wireOp",EDGE,"E47"),sQuery(id+"F11.wireOp",EDGE,"E52.2.0")])]})});
            var Q12;
            Q12=makeQuery(id+"F16.boolean.opBoolean","COPY",EDGE,{"derivedFrom":makeQuery(id+"F16.opExtrude","SWEPT_EDGE",EDGE,{"disambiguationData":[OSD([sQuery(id+"F11.wireOp",EDGE,"E47"),sQuery(id+"F11.wireOp",EDGE,"E52.3.1")])]})});
            var Q13;
            Q13=makeQuery(id+"F16.boolean.opBoolean","COPY",EDGE,{"derivedFrom":makeQuery(id+"F16.opExtrude","SWEPT_EDGE",EDGE,{"disambiguationData":[OSD([sQuery(id+"F11.wireOp",EDGE,"E47"),sQuery(id+"F11.wireOp",EDGE,"E50")])]})});
            var Q14;
            Q14=makeQuery(id+"F16.boolean.opBoolean","COPY",EDGE,{"derivedFrom":makeQuery(id+"F16.opExtrude","SWEPT_EDGE",EDGE,{"disambiguationData":[OSD([sQuery(id+"F11.wireOp",EDGE,"E47"),sQuery(id+"F11.wireOp",EDGE,"E52.3.0")])]})});
            var Q15;
            Q15=makeQuery(id+"F16.boolean.opBoolean","COPY",EDGE,{"derivedFrom":makeQuery(id+"F16.opExtrude","SWEPT_EDGE",EDGE,{"disambiguationData":[OSD([sQuery(id+"F11.wireOp",EDGE,"E47"),sQuery(id+"F11.wireOp",EDGE,"E49")])]})});
            fillet(context, id + "F17", {"entities" : qUnion([Q0, Q1, Q2, Q3, Q4, Q5, Q6, Q7, Q8, Q9, Q10, Q11, Q12, Q13, Q14, Q15]), "radius" : 2 * mm, "tangentPropagation" : true, "allowEdgeOverflow" : false});
        }
        {
            var Q0;
            Q0=makeQuery(id+"F12.imprint","IMPRINT",FACE,{"disambiguationData":[TD([[makeQuery(id+"F12.imprint","IMPRINT",EDGE,{"derivedFrom":makeQuery(id+"F10.opRevolve","SWEPT_EDGE",EDGE,{"disambiguationData":[OSD([sQuery(id+"F9.wireOp",EDGE,"E41"),sQuery(id+"F9.wireOp",EDGE,"E42")])]})}),-1.0]])]});
            extrude(context, id + "F18", {"entities" : qUnion([Q0]), "operationType" : NewBodyOperationType.REMOVE, "oppositeDirection" : true, "depth" : 45.2 * mm, "hasSecondDirection" : true, "secondDirectionOppositeDirection" : true, "secondDirectionDepth" : 2.54 * mm});
        }
    });
